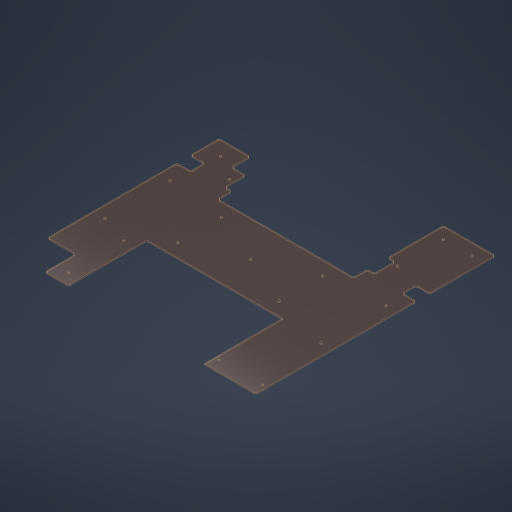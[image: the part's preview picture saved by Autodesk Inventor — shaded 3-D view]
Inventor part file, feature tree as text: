
AUTODESK INVENTOR PART (.ipt)
format: ipt  version: 2023.4 (Build 274418000, 418)  size: 399,360 bytes
history: native  units: in
note: dims shown in document units (in); Inventor stores cm internally (conversion verified against a paired STEP export)
features: sketch x4, extrude x3, projected_geometry x3, fillet x2, hole x1
ambient origin geometry x8: Origin, YZ Plane, XZ Plane, XY Plane, X Axis, Y Axis, Z Axis, Center Point
bodies: Solid1 (feature_tree)
feature tree (13):
  extrude  "Extrusion1"  Depth=25.97in
  extrude  "Extrusion2"  Depth=9.75in
  fillet  "Fillet1"  Radius=14.75in
  hole  "Hole1"  [1 undecoded]
  extrude  "Extrusion4"  Depth=2.25in
  fillet  "Fillet2"  Radius=2.1255in
  sketch  "Sketch1"  dims[d0=25.97in d1=25.97in]
  sketch  "Sketch2"  dims[d3=8.5in d4=9.75in d5=14.75in]
  sketch  "Sketch4"  dims[d6=0.125in d7=0.0in d8=0.225in]
  sketch  "Sketch5"  dims[d9=2.75in d10=1.831in d11=2.1255in d12=4.0in d14=0.0in d15=0.0in d16=0.75in d17=18.125in d18=1.5in d19=1.5in d20=2.5in d21=2.5in d28=1.5in d29=1.25in d30=4.75in d31=2.25in d32=2.0in d33=4.75in d34=1.25in d35=1.25in d36=1.25in d37=1.25in d38=1.25in d39=2.0in d40=1.875in d41=1.5in d42=1.5in d43=1.875in d44=1.25in d47=1.25in d48=1.25in d49=1.25in d50=2.0in d51=1.25in d52=0.201in d53=0.75in d54=0.385in d55=0.25in d56=0.5635in d57=0.12in d58=0.0in d59=5.0in d60=1.25in d61=4.0in d62=2.75in d63=1.5869in d64=1.3213in d65=0.375in d66=0.375in d67=0.0in d68=0.0in d69=0.225in d70=0.75in d71=2.25in]
  projected_geometry  "Project Cut Edges1"
  projected_geometry  "Project Cut Edges3"
  projected_geometry  "Project Cut Edges4"
note: 1 required parameter value undecoded (feature->parameter linkage not recoverable at this tier; creation-order binding heuristic only, values carry confidence <= 0.55)
